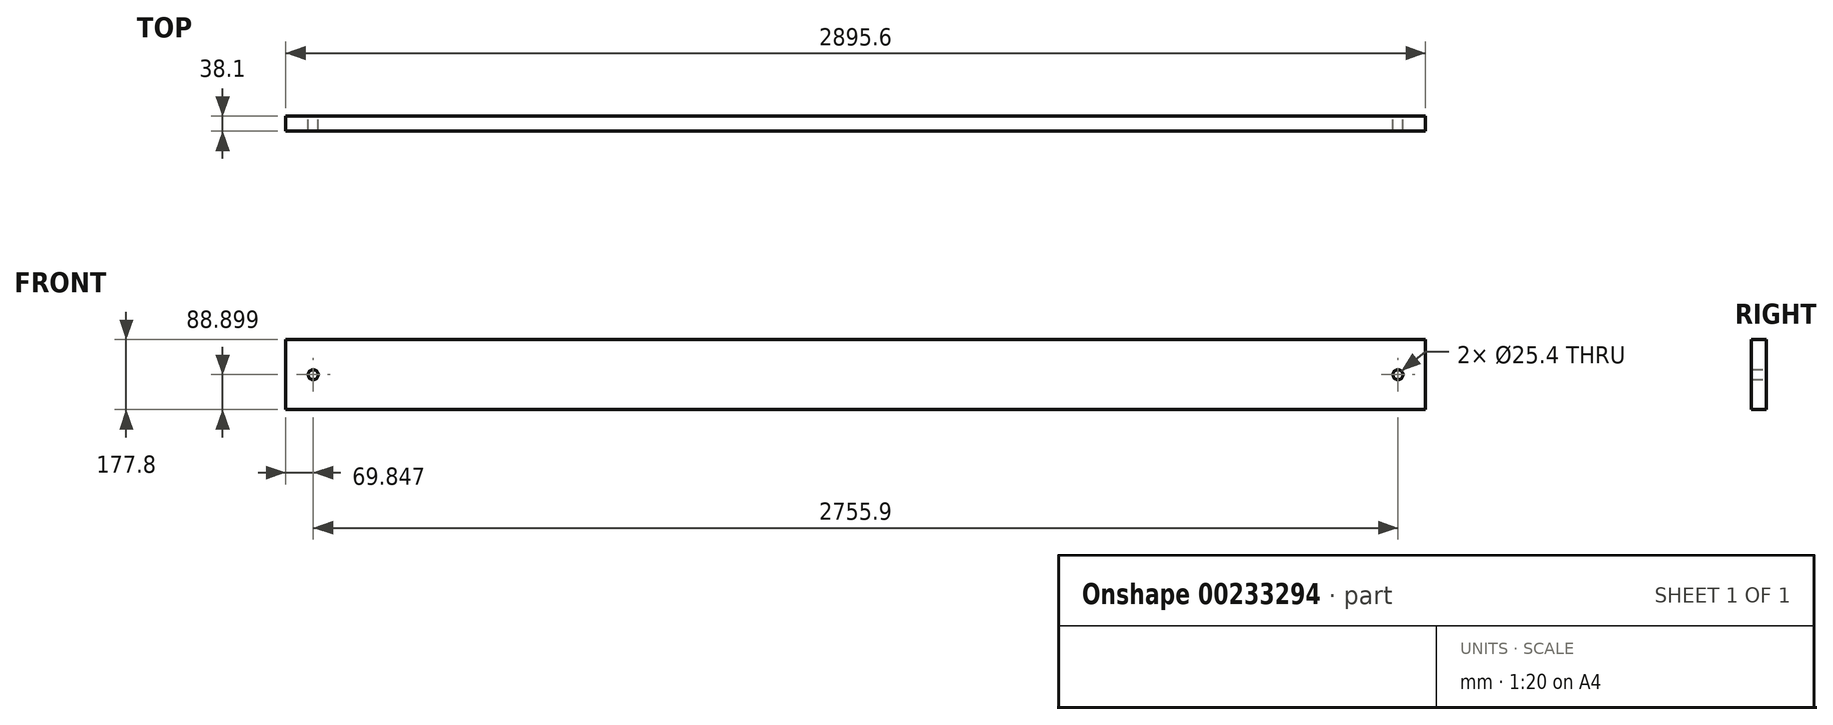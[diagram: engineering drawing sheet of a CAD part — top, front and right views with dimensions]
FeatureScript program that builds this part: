
annotation { "Feature Type Name" : "Feature", "Feature Type Description" : "" }
export const myFeature = defineFeature(function(context is Context, id is Id, definition is map)
    precondition{}
    {
        {
            var Q0;
            Q0=qCreatedBy(makeId("Front.planeOp"),FACE);
            var sketch = newSketch(context, id + "F0", { "sketchPlane" : qUnion([Q0])});
            skLineSegment(sketch, "E0.bottom", {"start": v(-1447.42, -362.17) * mm, "end": v(1448.18, -362.17) * mm});
            skLineSegment(sketch, "E0.top", {"start": v(-1447.42, -539.97) * mm, "end": v(1448.18, -539.97) * mm});
            skLineSegment(sketch, "E0.left", {"start": v(-1447.42, -362.17) * mm, "end": v(-1447.42, -539.97) * mm});
            skLineSegment(sketch, "E0.right", {"start": v(1448.18, -362.17) * mm, "end": v(1448.18, -539.97) * mm});
            skCircle(sketch, "E1", {"center": v(-1377.57, -451.07) * mm, "radius": 12.7 * mm});
            skCircle(sketch, "E2", {"center": v(1378.33, -451.07) * mm, "radius": 12.7 * mm});
            skSolve(sketch);
        }
        {
            var Q0;
            Q0 = qSketchRegion(id + "F0", true);
            extrude(context, id + "F1", {"entities" : qUnion([Q0]), "depth" : 38.1 * mm});
        }
    });
